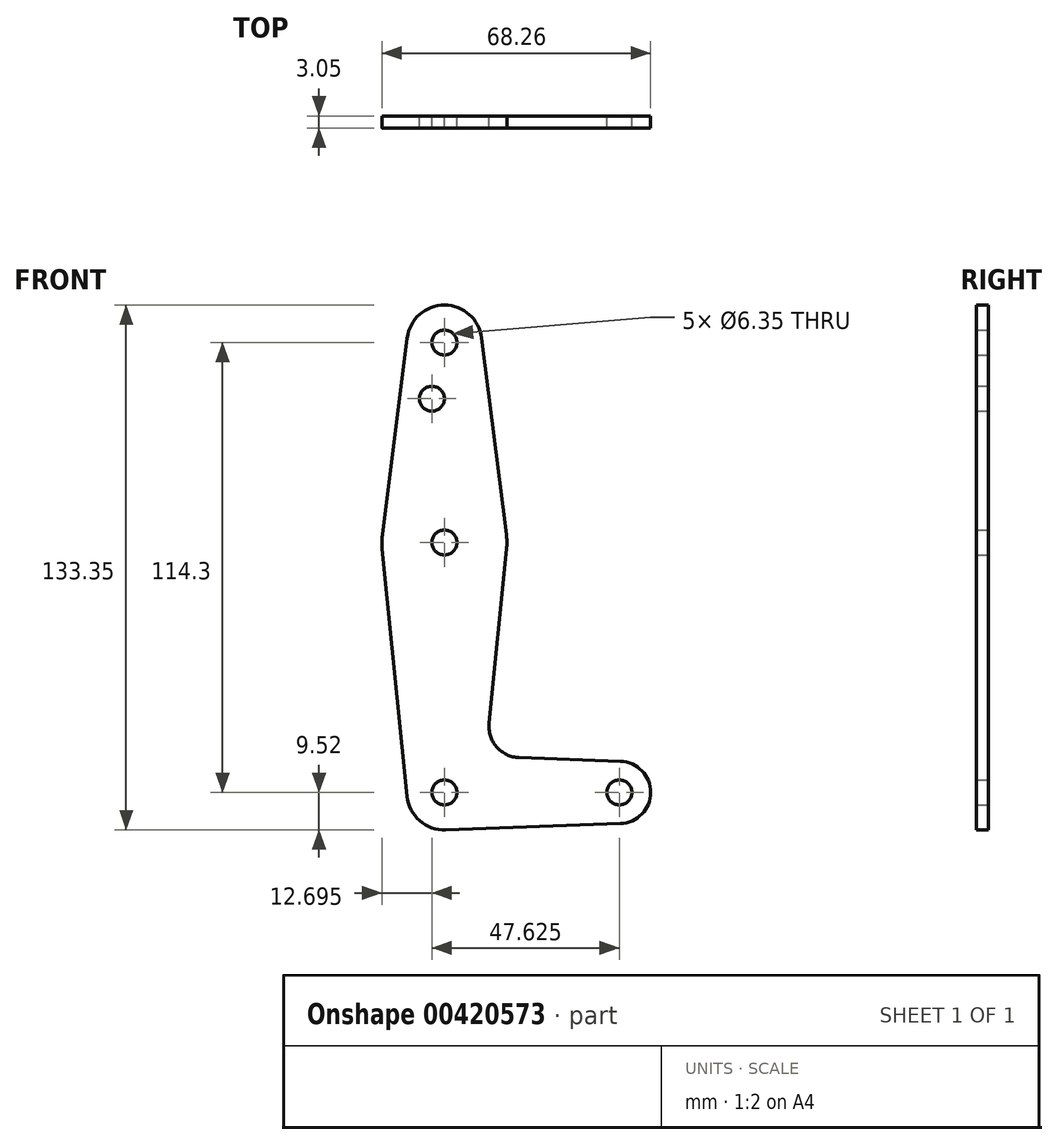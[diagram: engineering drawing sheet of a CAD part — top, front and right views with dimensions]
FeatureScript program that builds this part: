
annotation { "Feature Type Name" : "Feature", "Feature Type Description" : "" }
export const myFeature = defineFeature(function(context is Context, id is Id, definition is map)
    precondition{}
    {
        {
            var Q0;
            Q0=qCreatedBy(makeId("Front.planeOp"),FACE);
            var sketch = newSketch(context, id + "F0", { "sketchPlane" : qUnion([Q0])});
            skLineSegment(sketch, "E0", {"start": v(44.45, 0) * mm, "end": v(0, 0) * mm, "construction": true});
            skLineSegment(sketch, "E1", {"start": v(0, 0) * mm, "end": v(0, 114.3) * mm, "construction": true});
            skCircle(sketch, "E2", {"center": v(44.45, 0) * mm, "radius": 7.94 * mm});
            skCircle(sketch, "E3", {"center": v(0, 0) * mm, "radius": 9.53 * mm});
            skCircle(sketch, "E4", {"center": v(0, 63.5) * mm, "radius": 15.88 * mm});
            skCircle(sketch, "E5", {"center": v(0, 114.3) * mm, "radius": 9.53 * mm});
            skLineSegment(sketch, "E6", {"start": v(-9.48, -0.95) * mm, "end": v(-15.8, 61.91) * mm});
            skLineSegment(sketch, "E7", {"start": v(15.8, 61.91) * mm, "end": v(11.34, 17.6) * mm});
            skLineSegment(sketch, "E8", {"start": v(-15.75, 65.48) * mm, "end": v(-9.45, 115.5) * mm});
            skLineSegment(sketch, "E9", {"start": v(15.75, 65.48) * mm, "end": v(9.45, 115.5) * mm});
            skCircle(sketch, "E10", {"center": v(0, 114.3) * mm, "radius": 3.18 * mm});
            skCircle(sketch, "E11", {"center": v(0, 63.5) * mm, "radius": 3.18 * mm});
            skCircle(sketch, "E12", {"center": v(0, 0) * mm, "radius": 3.18 * mm});
            skCircle(sketch, "E13", {"center": v(44.45, 0) * mm, "radius": 3.18 * mm});
            skCircle(sketch, "E14", {"center": v(-3.18, 100.03) * mm, "radius": 3.18 * mm});
            skLineSegment(sketch, "E15", {"start": v(0.34, -9.52) * mm, "end": v(44.73, -7.93) * mm});
            skLineSegment(sketch, "E16", {"start": v(44.73, 7.93) * mm, "end": v(18.97, 8.85) * mm});
            skArc(sketch, "E17.filletArc", {"start": v(11.34, 17.6) * mm, "mid": v(13.26, 11.57) * mm, "end": v(18.97, 8.85) * mm});
            skSolve(sketch);
        }
        {
            var Q0;
            Q0=qSketchRegion(id+"F0",true);
            extrude(context, id + "F1", {"entities" : qUnion([Q0]), "depth" : 3.05 * mm});
        }
    });
